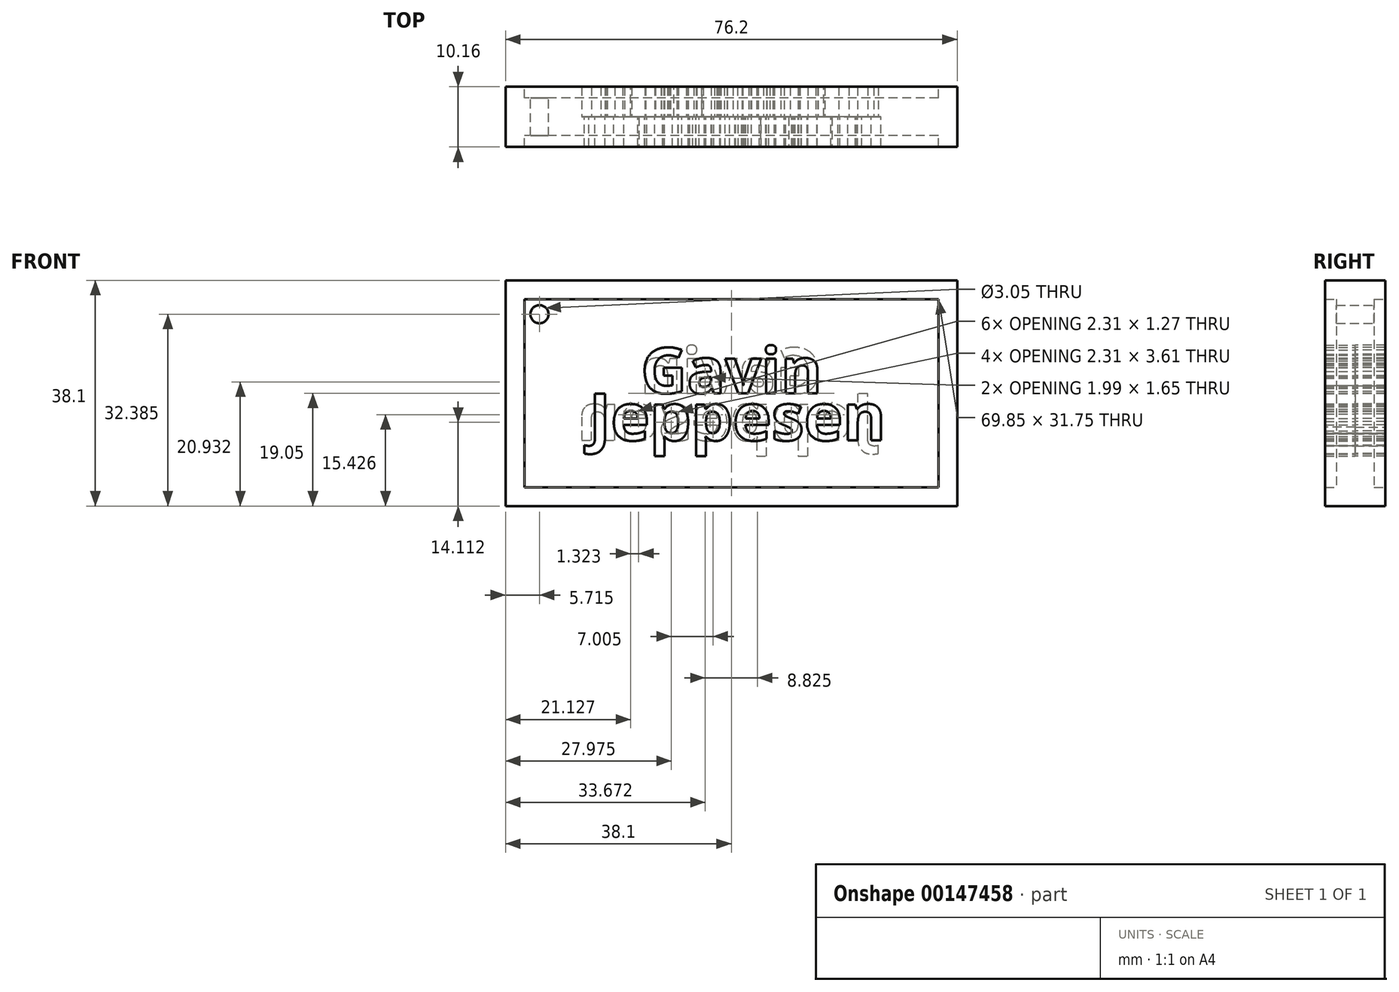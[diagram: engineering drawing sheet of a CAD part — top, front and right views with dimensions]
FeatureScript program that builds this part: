
annotation { "Feature Type Name" : "Feature", "Feature Type Description" : "" }
export const myFeature = defineFeature(function(context is Context, id is Id, definition is map)
    precondition{}
    {
        {
            var Q0;
            Q0=qCreatedBy(makeId("Front.planeOp"),FACE);
            var sketch = newSketch(context, id + "F0", { "sketchPlane" : qUnion([Q0])});
            skLineSegment(sketch, "E0.bottom", {"start": v(-38.1, 19.05) * mm, "end": v(38.1, 19.05) * mm});
            skLineSegment(sketch, "E0.top", {"start": v(-38.1, -19.05) * mm, "end": v(38.1, -19.05) * mm});
            skLineSegment(sketch, "E0.left", {"start": v(-38.1, 19.05) * mm, "end": v(-38.1, -19.05) * mm});
            skLineSegment(sketch, "E0.right", {"start": v(38.1, 19.05) * mm, "end": v(38.1, -19.05) * mm});
            skLineSegment(sketch, "E1.bottom", {"start": v(34.93, 15.88) * mm, "end": v(-34.93, 15.88) * mm});
            skLineSegment(sketch, "E1.top", {"start": v(34.93, -15.88) * mm, "end": v(-34.93, -15.88) * mm});
            skLineSegment(sketch, "E1.left", {"start": v(34.93, 15.88) * mm, "end": v(34.93, -15.88) * mm});
            skLineSegment(sketch, "E1.right", {"start": v(-34.93, 15.88) * mm, "end": v(-34.93, -15.88) * mm});
            skPoint(sketch, "E2", {"position": v(-32.39, 13.34) * mm});
            skSolve(sketch);
        }
        {
            var Q0;
            Q0=qCreatedBy(makeId("Front.planeOp"),FACE);
            var sketch = newSketch(context, id + "F1", { "sketchPlane" : qUnion([Q0])});
            skText(sketch, "E3", { "text": "Gavin", "fontName": "OpenSans-Bold.ttf"});
            skText(sketch, "E4", { "text": "Jeppesen", "fontName": "OpenSans-Bold.ttf"});
            const initialGuessF1  = {"E3": [-0.01525, 0, 1, 0, 0.0077], "E4": [-0.024, -0.00797, 1, 0, 0.00797]};
            skSetInitialGuess(sketch, initialGuessF1);
            skSolve(sketch);
        }
        {
            var Q0;
            Q0=makeQuery(id+"F0.imprint","IMPRINT",FACE,{"disambiguationData":[TD([[makeQuery(id+"F0.imprint","IMPRINT",EDGE,{"derivedFrom":sQuery(id+"F0.wireOp",EDGE,"E0.bottom")}),-1.0]])]});
            extrude(context, id + "F2", {"entities" : qUnion([Q0]), "endBound" : BoundingType.SYMMETRIC, "depth" : 10.16 * mm});
        }
        {
            var Q0;
            Q0=makeQuery(id+"F0.imprint","IMPRINT",FACE,{"disambiguationData":[TD([[makeQuery(id+"F0.imprint","IMPRINT",EDGE,{"derivedFrom":sQuery(id+"F0.wireOp",EDGE,"E1.bottom")}),1.0]])]});
            extrude(context, id + "F3", {"entities" : qUnion([Q0]), "operationType" : NewBodyOperationType.ADD, "endBound" : BoundingType.SYMMETRIC, "depth" : 6.35 * mm});
        }
        {
            var Q0;
            Q0 = qSketchRegion(id + "F1", true);
            extrude(context, id + "F4", {"entities" : qUnion([Q0]), "depth" : 5.08 * mm});
        }
        {
            var Q0;
            Q0=makeQuery(id+"F4.opExtrude","SWEPT_BODY",BODY,{"disambiguationData":[OSD([sQuery(id+"F1.wireOp",EDGE,"E3.sketch_text.stroke-0"),sQuery(id+"F1.wireOp",EDGE,"E3.sketch_text.stroke-1"),sQuery(id+"F1.wireOp",EDGE,"E3.sketch_text.stroke-2"),sQuery(id+"F1.wireOp",EDGE,"E3.sketch_text.stroke-3"),sQuery(id+"F1.wireOp",EDGE,"E3.sketch_text.stroke-4"),sQuery(id+"F1.wireOp",EDGE,"E3.sketch_text.stroke-5"),sQuery(id+"F1.wireOp",EDGE,"E3.sketch_text.stroke-6"),sQuery(id+"F1.wireOp",EDGE,"E3.sketch_text.stroke-7"),sQuery(id+"F1.wireOp",EDGE,"E3.sketch_text.stroke-8"),sQuery(id+"F1.wireOp",EDGE,"E3.sketch_text.stroke-9"),sQuery(id+"F1.wireOp",EDGE,"E3.sketch_text.stroke-10"),sQuery(id+"F1.wireOp",EDGE,"E3.sketch_text.stroke-11"),sQuery(id+"F1.wireOp",EDGE,"E3.sketch_text.stroke-12"),sQuery(id+"F1.wireOp",EDGE,"E3.sketch_text.stroke-13"),sQuery(id+"F1.wireOp",EDGE,"E3.sketch_text.stroke-14"),sQuery(id+"F1.wireOp",EDGE,"E3.sketch_text.stroke-15"),sQuery(id+"F1.wireOp",EDGE,"E3.sketch_text.stroke-16"),sQuery(id+"F1.wireOp",EDGE,"E3.sketch_text.stroke-17"),sQuery(id+"F1.wireOp",EDGE,"E3.sketch_text.stroke-18")])]});
            var Q1;
            Q1=makeQuery(id+"F4.opExtrude","SWEPT_BODY",BODY,{"disambiguationData":[OSD([sQuery(id+"F1.wireOp",EDGE,"E3.sketch_text.stroke-19"),sQuery(id+"F1.wireOp",EDGE,"E3.sketch_text.stroke-20"),sQuery(id+"F1.wireOp",EDGE,"E3.sketch_text.stroke-21"),sQuery(id+"F1.wireOp",EDGE,"E3.sketch_text.stroke-22"),sQuery(id+"F1.wireOp",EDGE,"E3.sketch_text.stroke-23"),sQuery(id+"F1.wireOp",EDGE,"E3.sketch_text.stroke-24"),sQuery(id+"F1.wireOp",EDGE,"E3.sketch_text.stroke-25"),sQuery(id+"F1.wireOp",EDGE,"E3.sketch_text.stroke-26"),sQuery(id+"F1.wireOp",EDGE,"E3.sketch_text.stroke-27"),sQuery(id+"F1.wireOp",EDGE,"E3.sketch_text.stroke-28"),sQuery(id+"F1.wireOp",EDGE,"E3.sketch_text.stroke-29"),sQuery(id+"F1.wireOp",EDGE,"E3.sketch_text.stroke-30"),sQuery(id+"F1.wireOp",EDGE,"E3.sketch_text.stroke-31"),sQuery(id+"F1.wireOp",EDGE,"E3.sketch_text.stroke-32"),sQuery(id+"F1.wireOp",EDGE,"E3.sketch_text.stroke-33"),sQuery(id+"F1.wireOp",EDGE,"E3.sketch_text.stroke-34"),sQuery(id+"F1.wireOp",EDGE,"E3.sketch_text.stroke-35"),sQuery(id+"F1.wireOp",EDGE,"E3.sketch_text.stroke-36"),sQuery(id+"F1.wireOp",EDGE,"E3.sketch_text.stroke-37"),sQuery(id+"F1.wireOp",EDGE,"E3.sketch_text.stroke-38"),sQuery(id+"F1.wireOp",EDGE,"E3.sketch_text.stroke-39"),sQuery(id+"F1.wireOp",EDGE,"E3.sketch_text.stroke-40"),sQuery(id+"F1.wireOp",EDGE,"E3.sketch_text.stroke-41"),sQuery(id+"F1.wireOp",EDGE,"E3.sketch_text.stroke-42"),sQuery(id+"F1.wireOp",EDGE,"E3.sketch_text.stroke-43")])]});
            var Q2;
            Q2=makeQuery(id+"F4.opExtrude","SWEPT_BODY",BODY,{"disambiguationData":[OSD([sQuery(id+"F1.wireOp",EDGE,"E3.sketch_text.stroke-44"),sQuery(id+"F1.wireOp",EDGE,"E3.sketch_text.stroke-45"),sQuery(id+"F1.wireOp",EDGE,"E3.sketch_text.stroke-46"),sQuery(id+"F1.wireOp",EDGE,"E3.sketch_text.stroke-47"),sQuery(id+"F1.wireOp",EDGE,"E3.sketch_text.stroke-48"),sQuery(id+"F1.wireOp",EDGE,"E3.sketch_text.stroke-49"),sQuery(id+"F1.wireOp",EDGE,"E3.sketch_text.stroke-50"),sQuery(id+"F1.wireOp",EDGE,"E3.sketch_text.stroke-51"),sQuery(id+"F1.wireOp",EDGE,"E3.sketch_text.stroke-52"),sQuery(id+"F1.wireOp",EDGE,"E3.sketch_text.stroke-53")])]});
            var Q3;
            Q3=makeQuery(id+"F4.opExtrude","SWEPT_BODY",BODY,{"disambiguationData":[OSD([sQuery(id+"F1.wireOp",EDGE,"E3.sketch_text.stroke-59"),sQuery(id+"F1.wireOp",EDGE,"E3.sketch_text.stroke-60"),sQuery(id+"F1.wireOp",EDGE,"E3.sketch_text.stroke-61"),sQuery(id+"F1.wireOp",EDGE,"E3.sketch_text.stroke-62")])]});
            var Q4;
            Q4=makeQuery(id+"F4.opExtrude","SWEPT_BODY",BODY,{"disambiguationData":[OSD([sQuery(id+"F1.wireOp",EDGE,"E3.sketch_text.stroke-63"),sQuery(id+"F1.wireOp",EDGE,"E3.sketch_text.stroke-64"),sQuery(id+"F1.wireOp",EDGE,"E3.sketch_text.stroke-65"),sQuery(id+"F1.wireOp",EDGE,"E3.sketch_text.stroke-66"),sQuery(id+"F1.wireOp",EDGE,"E3.sketch_text.stroke-67"),sQuery(id+"F1.wireOp",EDGE,"E3.sketch_text.stroke-68"),sQuery(id+"F1.wireOp",EDGE,"E3.sketch_text.stroke-69"),sQuery(id+"F1.wireOp",EDGE,"E3.sketch_text.stroke-70"),sQuery(id+"F1.wireOp",EDGE,"E3.sketch_text.stroke-71"),sQuery(id+"F1.wireOp",EDGE,"E3.sketch_text.stroke-72"),sQuery(id+"F1.wireOp",EDGE,"E3.sketch_text.stroke-73"),sQuery(id+"F1.wireOp",EDGE,"E3.sketch_text.stroke-74"),sQuery(id+"F1.wireOp",EDGE,"E3.sketch_text.stroke-75"),sQuery(id+"F1.wireOp",EDGE,"E3.sketch_text.stroke-76"),sQuery(id+"F1.wireOp",EDGE,"E3.sketch_text.stroke-77"),sQuery(id+"F1.wireOp",EDGE,"E3.sketch_text.stroke-78"),sQuery(id+"F1.wireOp",EDGE,"E3.sketch_text.stroke-79")])]});
            var Q5;
            Q5=makeQuery(id+"F4.opExtrude","SWEPT_BODY",BODY,{"disambiguationData":[OSD([sQuery(id+"F1.wireOp",EDGE,"E3.sketch_text.stroke-54"),sQuery(id+"F1.wireOp",EDGE,"E3.sketch_text.stroke-55"),sQuery(id+"F1.wireOp",EDGE,"E3.sketch_text.stroke-56"),sQuery(id+"F1.wireOp",EDGE,"E3.sketch_text.stroke-57"),sQuery(id+"F1.wireOp",EDGE,"E3.sketch_text.stroke-58")])]});
            var Q6;
            Q6=makeQuery(id+"F4.opExtrude","SWEPT_BODY",BODY,{"disambiguationData":[OSD([sQuery(id+"F1.wireOp",EDGE,"E4.sketch_text.stroke-142"),sQuery(id+"F1.wireOp",EDGE,"E4.sketch_text.stroke-143"),sQuery(id+"F1.wireOp",EDGE,"E4.sketch_text.stroke-144"),sQuery(id+"F1.wireOp",EDGE,"E4.sketch_text.stroke-145"),sQuery(id+"F1.wireOp",EDGE,"E4.sketch_text.stroke-146"),sQuery(id+"F1.wireOp",EDGE,"E4.sketch_text.stroke-147"),sQuery(id+"F1.wireOp",EDGE,"E4.sketch_text.stroke-148"),sQuery(id+"F1.wireOp",EDGE,"E4.sketch_text.stroke-149"),sQuery(id+"F1.wireOp",EDGE,"E4.sketch_text.stroke-150"),sQuery(id+"F1.wireOp",EDGE,"E4.sketch_text.stroke-151"),sQuery(id+"F1.wireOp",EDGE,"E4.sketch_text.stroke-152"),sQuery(id+"F1.wireOp",EDGE,"E4.sketch_text.stroke-153"),sQuery(id+"F1.wireOp",EDGE,"E4.sketch_text.stroke-154"),sQuery(id+"F1.wireOp",EDGE,"E4.sketch_text.stroke-155"),sQuery(id+"F1.wireOp",EDGE,"E4.sketch_text.stroke-156"),sQuery(id+"F1.wireOp",EDGE,"E4.sketch_text.stroke-157"),sQuery(id+"F1.wireOp",EDGE,"E4.sketch_text.stroke-158")])]});
            var Q7;
            Q7=makeQuery(id+"F4.opExtrude","SWEPT_BODY",BODY,{"disambiguationData":[OSD([sQuery(id+"F1.wireOp",EDGE,"E4.sketch_text.stroke-122"),sQuery(id+"F1.wireOp",EDGE,"E4.sketch_text.stroke-123"),sQuery(id+"F1.wireOp",EDGE,"E4.sketch_text.stroke-124"),sQuery(id+"F1.wireOp",EDGE,"E4.sketch_text.stroke-125"),sQuery(id+"F1.wireOp",EDGE,"E4.sketch_text.stroke-126"),sQuery(id+"F1.wireOp",EDGE,"E4.sketch_text.stroke-127"),sQuery(id+"F1.wireOp",EDGE,"E4.sketch_text.stroke-128"),sQuery(id+"F1.wireOp",EDGE,"E4.sketch_text.stroke-129"),sQuery(id+"F1.wireOp",EDGE,"E4.sketch_text.stroke-130"),sQuery(id+"F1.wireOp",EDGE,"E4.sketch_text.stroke-131"),sQuery(id+"F1.wireOp",EDGE,"E4.sketch_text.stroke-132"),sQuery(id+"F1.wireOp",EDGE,"E4.sketch_text.stroke-133"),sQuery(id+"F1.wireOp",EDGE,"E4.sketch_text.stroke-134"),sQuery(id+"F1.wireOp",EDGE,"E4.sketch_text.stroke-135"),sQuery(id+"F1.wireOp",EDGE,"E4.sketch_text.stroke-136"),sQuery(id+"F1.wireOp",EDGE,"E4.sketch_text.stroke-137"),sQuery(id+"F1.wireOp",EDGE,"E4.sketch_text.stroke-138"),sQuery(id+"F1.wireOp",EDGE,"E4.sketch_text.stroke-139"),sQuery(id+"F1.wireOp",EDGE,"E4.sketch_text.stroke-140"),sQuery(id+"F1.wireOp",EDGE,"E4.sketch_text.stroke-141")])]});
            var Q8;
            Q8=makeQuery(id+"F4.opExtrude","SWEPT_BODY",BODY,{"disambiguationData":[OSD([sQuery(id+"F1.wireOp",EDGE,"E4.sketch_text.stroke-96"),sQuery(id+"F1.wireOp",EDGE,"E4.sketch_text.stroke-97"),sQuery(id+"F1.wireOp",EDGE,"E4.sketch_text.stroke-98"),sQuery(id+"F1.wireOp",EDGE,"E4.sketch_text.stroke-99"),sQuery(id+"F1.wireOp",EDGE,"E4.sketch_text.stroke-100"),sQuery(id+"F1.wireOp",EDGE,"E4.sketch_text.stroke-101"),sQuery(id+"F1.wireOp",EDGE,"E4.sketch_text.stroke-102"),sQuery(id+"F1.wireOp",EDGE,"E4.sketch_text.stroke-103"),sQuery(id+"F1.wireOp",EDGE,"E4.sketch_text.stroke-104"),sQuery(id+"F1.wireOp",EDGE,"E4.sketch_text.stroke-105"),sQuery(id+"F1.wireOp",EDGE,"E4.sketch_text.stroke-106"),sQuery(id+"F1.wireOp",EDGE,"E4.sketch_text.stroke-107"),sQuery(id+"F1.wireOp",EDGE,"E4.sketch_text.stroke-108"),sQuery(id+"F1.wireOp",EDGE,"E4.sketch_text.stroke-109"),sQuery(id+"F1.wireOp",EDGE,"E4.sketch_text.stroke-110"),sQuery(id+"F1.wireOp",EDGE,"E4.sketch_text.stroke-111"),sQuery(id+"F1.wireOp",EDGE,"E4.sketch_text.stroke-112"),sQuery(id+"F1.wireOp",EDGE,"E4.sketch_text.stroke-113"),sQuery(id+"F1.wireOp",EDGE,"E4.sketch_text.stroke-114"),sQuery(id+"F1.wireOp",EDGE,"E4.sketch_text.stroke-115"),sQuery(id+"F1.wireOp",EDGE,"E4.sketch_text.stroke-116"),sQuery(id+"F1.wireOp",EDGE,"E4.sketch_text.stroke-117"),sQuery(id+"F1.wireOp",EDGE,"E4.sketch_text.stroke-118"),sQuery(id+"F1.wireOp",EDGE,"E4.sketch_text.stroke-119"),sQuery(id+"F1.wireOp",EDGE,"E4.sketch_text.stroke-120"),sQuery(id+"F1.wireOp",EDGE,"E4.sketch_text.stroke-121")])]});
            var Q9;
            Q9=makeQuery(id+"F4.opExtrude","SWEPT_BODY",BODY,{"disambiguationData":[OSD([sQuery(id+"F1.wireOp",EDGE,"E4.sketch_text.stroke-76"),sQuery(id+"F1.wireOp",EDGE,"E4.sketch_text.stroke-77"),sQuery(id+"F1.wireOp",EDGE,"E4.sketch_text.stroke-78"),sQuery(id+"F1.wireOp",EDGE,"E4.sketch_text.stroke-79"),sQuery(id+"F1.wireOp",EDGE,"E4.sketch_text.stroke-80"),sQuery(id+"F1.wireOp",EDGE,"E4.sketch_text.stroke-81"),sQuery(id+"F1.wireOp",EDGE,"E4.sketch_text.stroke-82"),sQuery(id+"F1.wireOp",EDGE,"E4.sketch_text.stroke-83"),sQuery(id+"F1.wireOp",EDGE,"E4.sketch_text.stroke-84"),sQuery(id+"F1.wireOp",EDGE,"E4.sketch_text.stroke-85"),sQuery(id+"F1.wireOp",EDGE,"E4.sketch_text.stroke-86"),sQuery(id+"F1.wireOp",EDGE,"E4.sketch_text.stroke-87"),sQuery(id+"F1.wireOp",EDGE,"E4.sketch_text.stroke-88"),sQuery(id+"F1.wireOp",EDGE,"E4.sketch_text.stroke-89"),sQuery(id+"F1.wireOp",EDGE,"E4.sketch_text.stroke-90"),sQuery(id+"F1.wireOp",EDGE,"E4.sketch_text.stroke-91"),sQuery(id+"F1.wireOp",EDGE,"E4.sketch_text.stroke-92"),sQuery(id+"F1.wireOp",EDGE,"E4.sketch_text.stroke-93"),sQuery(id+"F1.wireOp",EDGE,"E4.sketch_text.stroke-94"),sQuery(id+"F1.wireOp",EDGE,"E4.sketch_text.stroke-95")])]});
            var Q10;
            Q10=makeQuery(id+"F4.opExtrude","SWEPT_BODY",BODY,{"disambiguationData":[OSD([sQuery(id+"F1.wireOp",EDGE,"E4.sketch_text.stroke-53"),sQuery(id+"F1.wireOp",EDGE,"E4.sketch_text.stroke-54"),sQuery(id+"F1.wireOp",EDGE,"E4.sketch_text.stroke-55"),sQuery(id+"F1.wireOp",EDGE,"E4.sketch_text.stroke-56"),sQuery(id+"F1.wireOp",EDGE,"E4.sketch_text.stroke-57"),sQuery(id+"F1.wireOp",EDGE,"E4.sketch_text.stroke-58"),sQuery(id+"F1.wireOp",EDGE,"E4.sketch_text.stroke-59"),sQuery(id+"F1.wireOp",EDGE,"E4.sketch_text.stroke-60"),sQuery(id+"F1.wireOp",EDGE,"E4.sketch_text.stroke-61"),sQuery(id+"F1.wireOp",EDGE,"E4.sketch_text.stroke-62"),sQuery(id+"F1.wireOp",EDGE,"E4.sketch_text.stroke-63"),sQuery(id+"F1.wireOp",EDGE,"E4.sketch_text.stroke-64"),sQuery(id+"F1.wireOp",EDGE,"E4.sketch_text.stroke-65"),sQuery(id+"F1.wireOp",EDGE,"E4.sketch_text.stroke-66"),sQuery(id+"F1.wireOp",EDGE,"E4.sketch_text.stroke-67"),sQuery(id+"F1.wireOp",EDGE,"E4.sketch_text.stroke-68"),sQuery(id+"F1.wireOp",EDGE,"E4.sketch_text.stroke-69"),sQuery(id+"F1.wireOp",EDGE,"E4.sketch_text.stroke-70"),sQuery(id+"F1.wireOp",EDGE,"E4.sketch_text.stroke-71"),sQuery(id+"F1.wireOp",EDGE,"E4.sketch_text.stroke-72"),sQuery(id+"F1.wireOp",EDGE,"E4.sketch_text.stroke-73"),sQuery(id+"F1.wireOp",EDGE,"E4.sketch_text.stroke-74"),sQuery(id+"F1.wireOp",EDGE,"E4.sketch_text.stroke-75")])]});
            var Q11;
            Q11=makeQuery(id+"F4.opExtrude","SWEPT_BODY",BODY,{"disambiguationData":[OSD([sQuery(id+"F1.wireOp",EDGE,"E4.sketch_text.stroke-30"),sQuery(id+"F1.wireOp",EDGE,"E4.sketch_text.stroke-31"),sQuery(id+"F1.wireOp",EDGE,"E4.sketch_text.stroke-32"),sQuery(id+"F1.wireOp",EDGE,"E4.sketch_text.stroke-33"),sQuery(id+"F1.wireOp",EDGE,"E4.sketch_text.stroke-34"),sQuery(id+"F1.wireOp",EDGE,"E4.sketch_text.stroke-35"),sQuery(id+"F1.wireOp",EDGE,"E4.sketch_text.stroke-36"),sQuery(id+"F1.wireOp",EDGE,"E4.sketch_text.stroke-37"),sQuery(id+"F1.wireOp",EDGE,"E4.sketch_text.stroke-38"),sQuery(id+"F1.wireOp",EDGE,"E4.sketch_text.stroke-39"),sQuery(id+"F1.wireOp",EDGE,"E4.sketch_text.stroke-40"),sQuery(id+"F1.wireOp",EDGE,"E4.sketch_text.stroke-41"),sQuery(id+"F1.wireOp",EDGE,"E4.sketch_text.stroke-42"),sQuery(id+"F1.wireOp",EDGE,"E4.sketch_text.stroke-43"),sQuery(id+"F1.wireOp",EDGE,"E4.sketch_text.stroke-44"),sQuery(id+"F1.wireOp",EDGE,"E4.sketch_text.stroke-45"),sQuery(id+"F1.wireOp",EDGE,"E4.sketch_text.stroke-46"),sQuery(id+"F1.wireOp",EDGE,"E4.sketch_text.stroke-47"),sQuery(id+"F1.wireOp",EDGE,"E4.sketch_text.stroke-48"),sQuery(id+"F1.wireOp",EDGE,"E4.sketch_text.stroke-49"),sQuery(id+"F1.wireOp",EDGE,"E4.sketch_text.stroke-50"),sQuery(id+"F1.wireOp",EDGE,"E4.sketch_text.stroke-51"),sQuery(id+"F1.wireOp",EDGE,"E4.sketch_text.stroke-52")])]});
            var Q12;
            Q12=makeQuery(id+"F4.opExtrude","SWEPT_BODY",BODY,{"disambiguationData":[OSD([sQuery(id+"F1.wireOp",EDGE,"E4.sketch_text.stroke-10"),sQuery(id+"F1.wireOp",EDGE,"E4.sketch_text.stroke-11"),sQuery(id+"F1.wireOp",EDGE,"E4.sketch_text.stroke-12"),sQuery(id+"F1.wireOp",EDGE,"E4.sketch_text.stroke-13"),sQuery(id+"F1.wireOp",EDGE,"E4.sketch_text.stroke-14"),sQuery(id+"F1.wireOp",EDGE,"E4.sketch_text.stroke-15"),sQuery(id+"F1.wireOp",EDGE,"E4.sketch_text.stroke-16"),sQuery(id+"F1.wireOp",EDGE,"E4.sketch_text.stroke-17"),sQuery(id+"F1.wireOp",EDGE,"E4.sketch_text.stroke-18"),sQuery(id+"F1.wireOp",EDGE,"E4.sketch_text.stroke-19"),sQuery(id+"F1.wireOp",EDGE,"E4.sketch_text.stroke-20"),sQuery(id+"F1.wireOp",EDGE,"E4.sketch_text.stroke-21"),sQuery(id+"F1.wireOp",EDGE,"E4.sketch_text.stroke-22"),sQuery(id+"F1.wireOp",EDGE,"E4.sketch_text.stroke-23"),sQuery(id+"F1.wireOp",EDGE,"E4.sketch_text.stroke-24"),sQuery(id+"F1.wireOp",EDGE,"E4.sketch_text.stroke-25"),sQuery(id+"F1.wireOp",EDGE,"E4.sketch_text.stroke-26"),sQuery(id+"F1.wireOp",EDGE,"E4.sketch_text.stroke-27"),sQuery(id+"F1.wireOp",EDGE,"E4.sketch_text.stroke-28"),sQuery(id+"F1.wireOp",EDGE,"E4.sketch_text.stroke-29")])]});
            var Q13;
            Q13=makeQuery(id+"F4.opExtrude","SWEPT_BODY",BODY,{"disambiguationData":[OSD([sQuery(id+"F1.wireOp",EDGE,"E4.sketch_text.stroke-0"),sQuery(id+"F1.wireOp",EDGE,"E4.sketch_text.stroke-1"),sQuery(id+"F1.wireOp",EDGE,"E4.sketch_text.stroke-2"),sQuery(id+"F1.wireOp",EDGE,"E4.sketch_text.stroke-3"),sQuery(id+"F1.wireOp",EDGE,"E4.sketch_text.stroke-4"),sQuery(id+"F1.wireOp",EDGE,"E4.sketch_text.stroke-5"),sQuery(id+"F1.wireOp",EDGE,"E4.sketch_text.stroke-6"),sQuery(id+"F1.wireOp",EDGE,"E4.sketch_text.stroke-7"),sQuery(id+"F1.wireOp",EDGE,"E4.sketch_text.stroke-8"),sQuery(id+"F1.wireOp",EDGE,"E4.sketch_text.stroke-9")])]});
            var Q14;
            Q14=sQuery(id+"F1.wireOp",EDGE,"E3.sketch_text.center");
            transform(context, id + "F5", {"entities" : qUnion([Q0, Q1, Q2, Q3, Q4, Q5, Q6, Q7, Q8, Q9, Q10, Q11, Q12, Q13]), "transformType" : TransformType.ROTATION, "transformAxis" : qUnion([Q14]), "angle" : 180 * degree, "makeCopy" : true});
        }
        {
            var Q0;
            Q0=sQuery(id+"F0.wireOp",VERTEX,"E2");
            var Q1;
            Q1=makeQuery(id+"F2.opExtrude","SWEPT_BODY",BODY,{"disambiguationData":[OSD([sQuery(id+"F0.wireOp",EDGE,"E0.bottom"),sQuery(id+"F0.wireOp",EDGE,"E0.top"),sQuery(id+"F0.wireOp",EDGE,"E0.left"),sQuery(id+"F0.wireOp",EDGE,"E0.right"),sQuery(id+"F0.wireOp",EDGE,"E1.bottom"),sQuery(id+"F0.wireOp",EDGE,"E1.top"),sQuery(id+"F0.wireOp",EDGE,"E1.left"),sQuery(id+"F0.wireOp",EDGE,"E1.right")])]});
            hole(context, id + "F6", {"style" : HoleStyle.SIMPLE, "endStyle" : HoleEndStyle.THROUGH, "oppositeDirection" : true, "holeDiameter" : 3.05 * mm, "locations" : qUnion([Q0]), "scope" : qUnion([Q1]), "isTappedThrough" : true});
        }
        {
            var Q0;
            Q0=sQuery(id+"F0.wireOp",VERTEX,"E2");
            var Q1;
            Q1=makeQuery(id+"F2.opExtrude","SWEPT_BODY",BODY,{"disambiguationData":[OSD([sQuery(id+"F0.wireOp",EDGE,"E0.bottom"),sQuery(id+"F0.wireOp",EDGE,"E0.top"),sQuery(id+"F0.wireOp",EDGE,"E0.left"),sQuery(id+"F0.wireOp",EDGE,"E0.right"),sQuery(id+"F0.wireOp",EDGE,"E1.bottom"),sQuery(id+"F0.wireOp",EDGE,"E1.top"),sQuery(id+"F0.wireOp",EDGE,"E1.left"),sQuery(id+"F0.wireOp",EDGE,"E1.right")])]});
            hole(context, id + "F7", {"style" : HoleStyle.SIMPLE, "endStyle" : HoleEndStyle.THROUGH, "holeDiameter" : 3.05 * mm, "locations" : qUnion([Q0]), "scope" : qUnion([Q1]), "isTappedThrough" : true});
        }
    });
